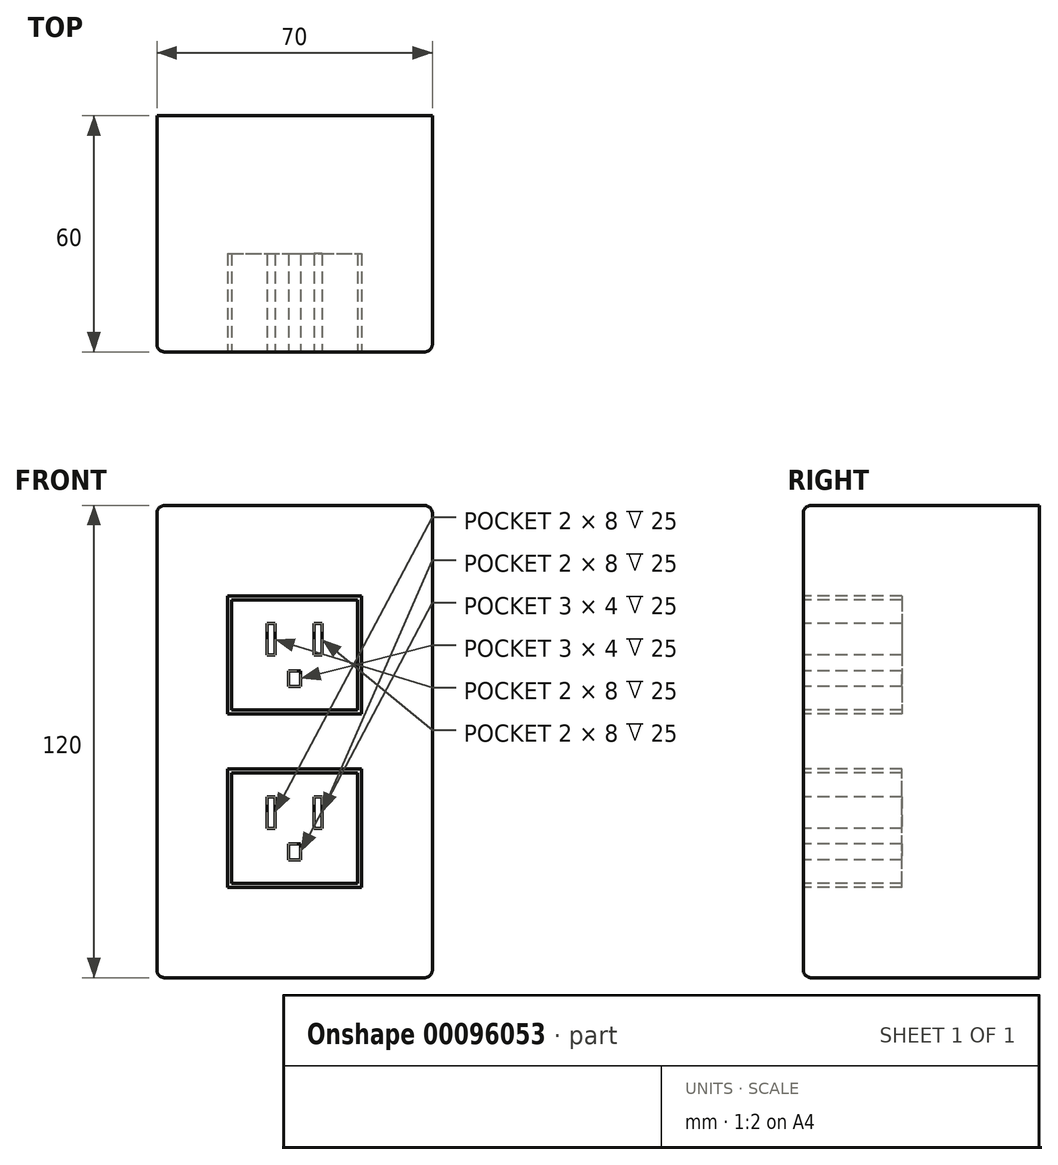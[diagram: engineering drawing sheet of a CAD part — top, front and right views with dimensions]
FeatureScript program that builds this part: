
annotation { "Feature Type Name" : "Feature", "Feature Type Description" : "" }
export const myFeature = defineFeature(function(context is Context, id is Id, definition is map)
    precondition{}
    {
        {
            var Q0;
            Q0=qCreatedBy(makeId("Front.planeOp"),FACE);
            var sketch = newSketch(context, id + "F0", { "sketchPlane" : qUnion([Q0])});
            skLineSegment(sketch, "E0.bottom", {"start": v(35, -60) * mm, "end": v(-35, -60) * mm});
            skLineSegment(sketch, "E0.top", {"start": v(35, 60) * mm, "end": v(-35, 60) * mm});
            skLineSegment(sketch, "E0.left", {"start": v(35, -60) * mm, "end": v(35, 60) * mm});
            skLineSegment(sketch, "E0.right", {"start": v(-35, -60) * mm, "end": v(-35, 60) * mm});
            skPoint(sketch, "E0.middle", {"position": v(0, 0) * mm});
            skSolve(sketch);
        }
        {
            var Q0;
            Q0 = qSketchRegion(id + "F0", true);
            extrude(context, id + "F1", {"entities" : qUnion([Q0]), "depth" : 60 * mm});
        }
        {
            var Q0;
            Q0=makeQuery(id+"F1.opExtrude","SWEPT_EDGE",EDGE,{"disambiguationData":[OSD([sQuery(id+"F0.wireOp",EDGE,"E0.top"),sQuery(id+"F0.wireOp",EDGE,"E0.left")])]});
            var Q1;
            Q1=makeQuery(id+"F1.opExtrude","SWEPT_EDGE",EDGE,{"disambiguationData":[OSD([sQuery(id+"F0.wireOp",EDGE,"E0.bottom"),sQuery(id+"F0.wireOp",EDGE,"E0.left")])]});
            var Q2;
            Q2=makeQuery(id+"F1.opExtrude","SWEPT_EDGE",EDGE,{"disambiguationData":[OSD([sQuery(id+"F0.wireOp",EDGE,"E0.top"),sQuery(id+"F0.wireOp",EDGE,"E0.right")])]});
            var Q3;
            Q3=makeQuery(id+"F1.opExtrude","SWEPT_EDGE",EDGE,{"disambiguationData":[OSD([sQuery(id+"F0.wireOp",EDGE,"E0.bottom"),sQuery(id+"F0.wireOp",EDGE,"E0.right")])]});
            var Q4;
            Q4=makeQuery(id+"F1.opExtrude","CAP_FACE",FACE,{"disambiguationData":[OSD([sQuery(id+"F0.wireOp",EDGE,"E0.bottom"),sQuery(id+"F0.wireOp",EDGE,"E0.top"),sQuery(id+"F0.wireOp",EDGE,"E0.left"),sQuery(id+"F0.wireOp",EDGE,"E0.right")])],"isStart":false});
            fillet(context, id + "F2", {"entities" : qUnion([Q0, Q1, Q2, Q3, Q4]), "radius" : 2 * mm, "tangentPropagation" : true, "allowEdgeOverflow" : false});
        }
        {
            var Q0;
            Q0=makeQuery(id+"F1.opExtrude","CAP_FACE",FACE,{"disambiguationData":[OSD([sQuery(id+"F0.wireOp",EDGE,"E0.bottom"),sQuery(id+"F0.wireOp",EDGE,"E0.top"),sQuery(id+"F0.wireOp",EDGE,"E0.left"),sQuery(id+"F0.wireOp",EDGE,"E0.right")])],"isStart":false});
            var sketch = newSketch(context, id + "F3", { "sketchPlane" : qUnion([Q0])});
            skLineSegment(sketch, "E1.bottom", {"start": v(-17, 37) * mm, "end": v(17, 37) * mm});
            skLineSegment(sketch, "E1.top", {"start": v(-17, 7) * mm, "end": v(17, 7) * mm});
            skLineSegment(sketch, "E1.left", {"start": v(-17, 37) * mm, "end": v(-17, 7) * mm});
            skLineSegment(sketch, "E1.right", {"start": v(17, 37) * mm, "end": v(17, 7) * mm});
            skLineSegment(sketch, "E2.0", {"start": v(-16, 36) * mm, "end": v(16, 36) * mm});
            skLineSegment(sketch, "E2.1", {"start": v(-16, 36) * mm, "end": v(-16, 8) * mm});
            skLineSegment(sketch, "E2.2", {"start": v(-16, 8) * mm, "end": v(16, 8) * mm});
            skLineSegment(sketch, "E2.3", {"start": v(16, 36) * mm, "end": v(16, 8) * mm});
            skLineSegment(sketch, "E3.MirrorCS", {"start": v(-17, -7) * mm, "end": v(17, -7) * mm});
            skLineSegment(sketch, "E4.MirrorCS", {"start": v(-16, -8) * mm, "end": v(16, -8) * mm});
            skLineSegment(sketch, "E5.MirrorCS", {"start": v(-16, -36) * mm, "end": v(16, -36) * mm});
            skLineSegment(sketch, "E6.MirrorCS", {"start": v(-17, -37) * mm, "end": v(17, -37) * mm});
            skLineSegment(sketch, "E7.MirrorCS", {"start": v(-16, -36) * mm, "end": v(-16, -8) * mm});
            skLineSegment(sketch, "E8.MirrorCS", {"start": v(-17, -37) * mm, "end": v(-17, -7) * mm});
            skLineSegment(sketch, "E9.MirrorCS", {"start": v(16, -36) * mm, "end": v(16, -8) * mm});
            skLineSegment(sketch, "E10.MirrorCS", {"start": v(17, -37) * mm, "end": v(17, -7) * mm});
            skSolve(sketch);
        }
        {
            var Q0;
            Q0 = qSketchRegion(id + "F3", true);
            extrude(context, id + "F4", {"entities" : qUnion([Q0]), "operationType" : NewBodyOperationType.REMOVE, "oppositeDirection" : true, "depth" : 25 * mm});
        }
        {
            var Q0;
            Q0=makeQuery(id+"F4.boolean.opBoolean","SPLIT",FACE,{"disambiguationData":[TD([makeQuery(id+"F4.opExtrude","SWEPT_FACE",FACE,{"disambiguationData":[OSD([sQuery(id+"F3.wireOp",EDGE,"E2.0")])]})])],"derivedFrom":makeQuery(id+"F1.opExtrude","CAP_FACE",FACE,{"disambiguationData":[OSD([sQuery(id+"F0.wireOp",EDGE,"E0.bottom"),sQuery(id+"F0.wireOp",EDGE,"E0.top"),sQuery(id+"F0.wireOp",EDGE,"E0.left"),sQuery(id+"F0.wireOp",EDGE,"E0.right")])],"isStart":false})});
            var sketch = newSketch(context, id + "F5", { "sketchPlane" : qUnion([Q0])});
            skLineSegment(sketch, "E11.bottom", {"start": v(1.5, 14) * mm, "end": v(-1.5, 14) * mm});
            skLineSegment(sketch, "E11.top", {"start": v(1.5, 18) * mm, "end": v(-1.5, 18) * mm});
            skLineSegment(sketch, "E11.left", {"start": v(1.5, 14) * mm, "end": v(1.5, 18) * mm});
            skLineSegment(sketch, "E11.right", {"start": v(-1.5, 14) * mm, "end": v(-1.5, 18) * mm});
            skPoint(sketch, "E11.middle", {"position": v(0, 16) * mm});
            skLineSegment(sketch, "E12.bottom", {"start": v(-1.5, -26) * mm, "end": v(1.5, -26) * mm});
            skLineSegment(sketch, "E12.top", {"start": v(-1.5, -30) * mm, "end": v(1.5, -30) * mm});
            skLineSegment(sketch, "E12.left", {"start": v(-1.5, -26) * mm, "end": v(-1.5, -30) * mm});
            skLineSegment(sketch, "E12.right", {"start": v(1.5, -26) * mm, "end": v(1.5, -30) * mm});
            skPoint(sketch, "E12.middle", {"position": v(0, -28) * mm});
            skLineSegment(sketch, "E13.bottom", {"start": v(-7, -14) * mm, "end": v(-5, -14) * mm});
            skLineSegment(sketch, "E13.top", {"start": v(-7, -22) * mm, "end": v(-5, -22) * mm});
            skLineSegment(sketch, "E13.left", {"start": v(-7, -14) * mm, "end": v(-7, -22) * mm});
            skLineSegment(sketch, "E13.right", {"start": v(-5, -14) * mm, "end": v(-5, -22) * mm});
            skLineSegment(sketch, "E14.bottom", {"start": v(-7, 30) * mm, "end": v(-5, 30) * mm});
            skLineSegment(sketch, "E14.top", {"start": v(-7, 22) * mm, "end": v(-5, 22) * mm});
            skLineSegment(sketch, "E14.left", {"start": v(-7, 30) * mm, "end": v(-7, 22) * mm});
            skLineSegment(sketch, "E14.right", {"start": v(-5, 30) * mm, "end": v(-5, 22) * mm});
            skLineSegment(sketch, "E15.MirrorCS", {"start": v(7, 30) * mm, "end": v(5, 30) * mm});
            skLineSegment(sketch, "E16.MirrorCS", {"start": v(5, 30) * mm, "end": v(5, 22) * mm});
            skLineSegment(sketch, "E17.MirrorCS", {"start": v(7, 22) * mm, "end": v(5, 22) * mm});
            skLineSegment(sketch, "E18.MirrorCS", {"start": v(7, 30) * mm, "end": v(7, 22) * mm});
            skLineSegment(sketch, "E19.MirrorCS", {"start": v(7, -14) * mm, "end": v(5, -14) * mm});
            skLineSegment(sketch, "E20.MirrorCS", {"start": v(7, -14) * mm, "end": v(7, -22) * mm});
            skLineSegment(sketch, "E21.MirrorCS", {"start": v(7, -22) * mm, "end": v(5, -22) * mm});
            skLineSegment(sketch, "E22.MirrorCS", {"start": v(5, -14) * mm, "end": v(5, -22) * mm});
            skSolve(sketch);
        }
        {
            var Q0;
            Q0 = qSketchRegion(id + "F5", true);
            extrude(context, id + "F6", {"entities" : qUnion([Q0]), "operationType" : NewBodyOperationType.REMOVE, "oppositeDirection" : true, "depth" : 25 * mm});
        }
    });
